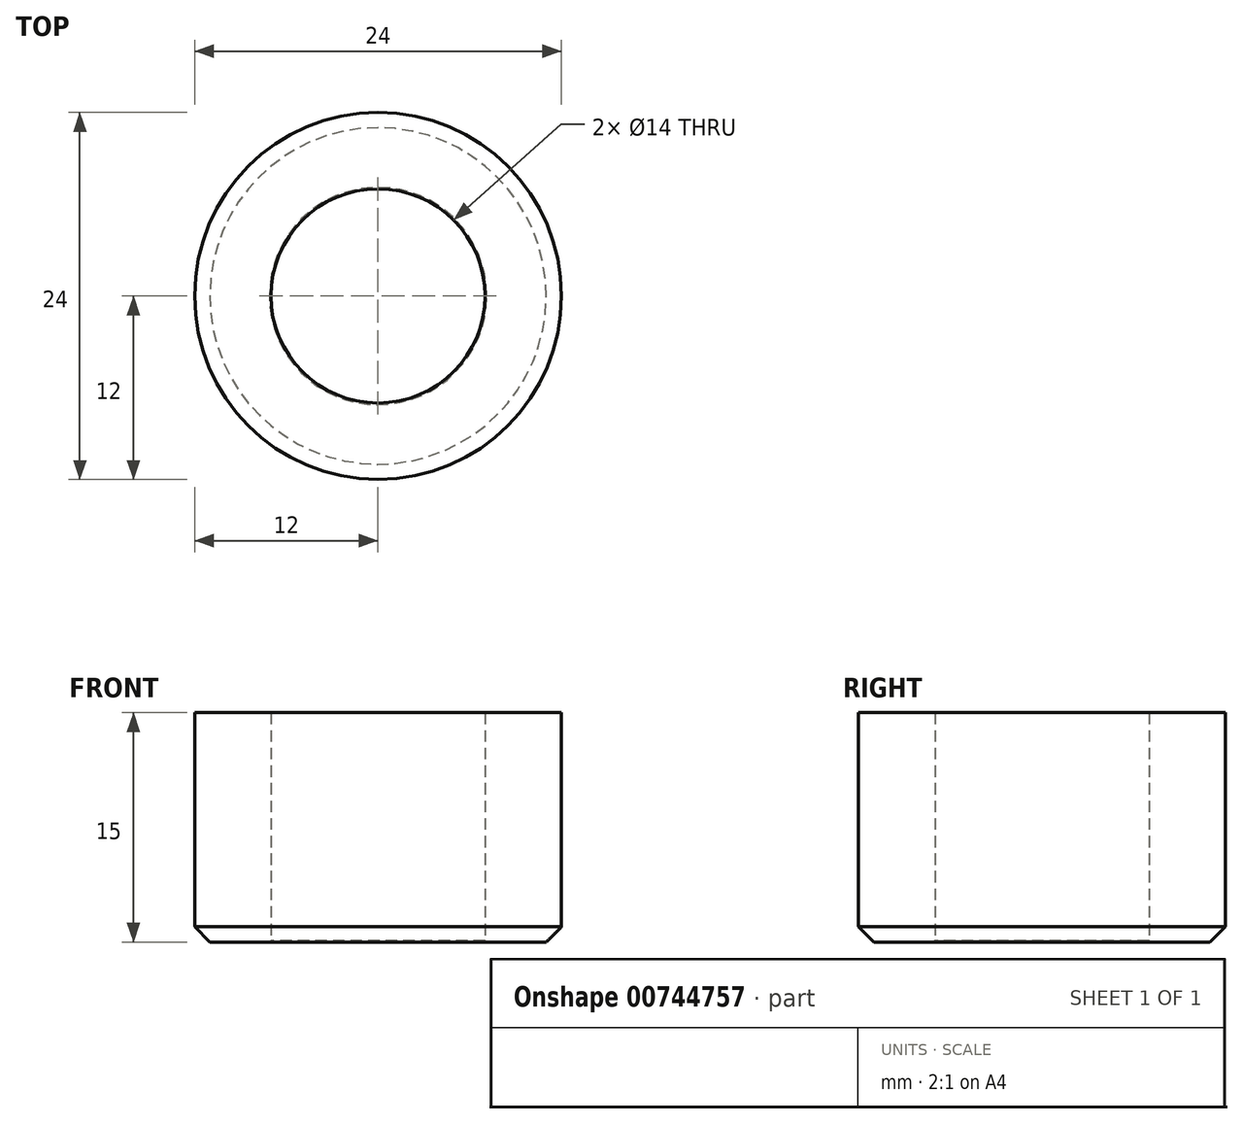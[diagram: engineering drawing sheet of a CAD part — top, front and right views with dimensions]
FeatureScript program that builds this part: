
annotation { "Feature Type Name" : "Feature", "Feature Type Description" : "" }
export const myFeature = defineFeature(function(context is Context, id is Id, definition is map)
    precondition{}
    {
        {
            var Q0;
            Q0=qCreatedBy(makeId("Top.planeOp"),FACE);
            var sketch = newSketch(context, id + "F0", { "sketchPlane" : qUnion([Q0])});
            skCircle(sketch, "E0", {"center": v(0, 0) * mm, "radius": 7 * mm});
            skCircle(sketch, "E1", {"center": v(0, 0) * mm, "radius": 12 * mm});
            skSolve(sketch);
        }
        {
            var Q0;
            Q0=makeQuery(id+"F0.imprint","IMPRINT",FACE,{"disambiguationData":[TD([[makeQuery(id+"F0.imprint","IMPRINT",EDGE,{"derivedFrom":sQuery(id+"F0.wireOp",EDGE,"E0")}),-1.0]])]});
            extrude(context, id + "F1", {"entities" : qUnion([Q0]), "depth" : 15 * mm, "offsetDistance" : 25 * mm});
        }
        {
            var Q0;
            Q0=makeQuery(id+"F1.opExtrude","CAP_EDGE",EDGE,{"disambiguationData":[OSD([sQuery(id+"F0.wireOp",EDGE,"E1")])],"isStart":true});
            chamfer(context, id + "F2", {"entities" : qUnion([Q0]), "width" : 1 * mm, "tangentPropagation" : true});
        }
        {
            var Q0;
            Q0=makeQuery(id+"F1.opExtrude","CAP_EDGE",EDGE,{"disambiguationData":[OSD([sQuery(id+"F0.wireOp",EDGE,"E0")])],"isStart":true});
            chamfer(context, id + "F3", {"entities" : qUnion([Q0]), "width" : .1 * mm, "tangentPropagation" : true});
        }
    });
